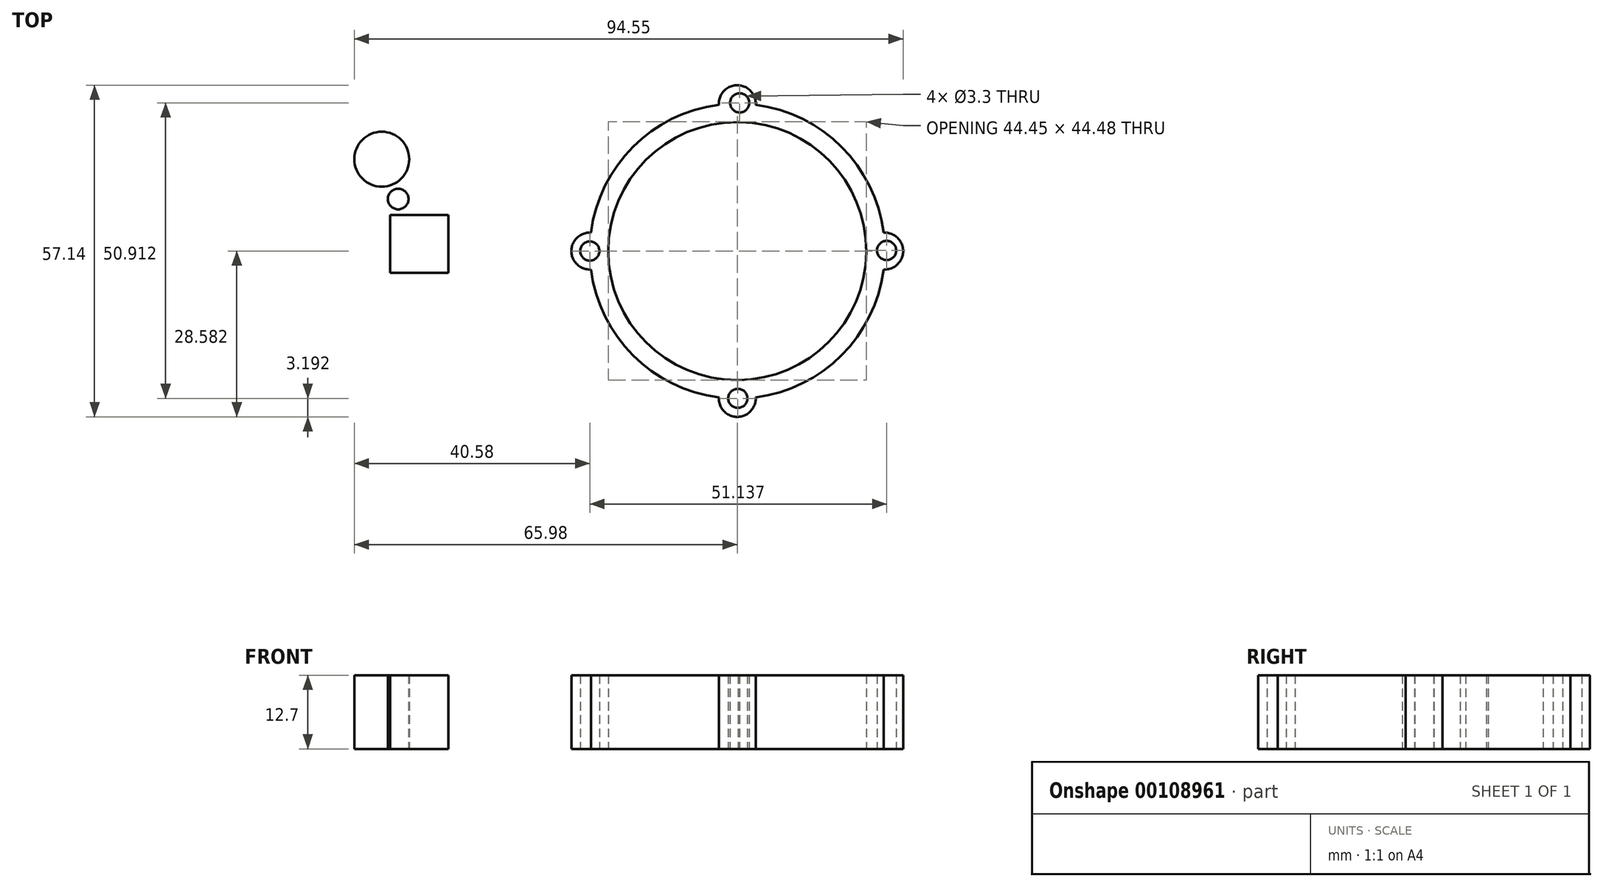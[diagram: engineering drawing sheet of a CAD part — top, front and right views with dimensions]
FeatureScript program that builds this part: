
annotation { "Feature Type Name" : "Feature", "Feature Type Description" : "" }
export const myFeature = defineFeature(function(context is Context, id is Id, definition is map)
    precondition{}
    {
        {
            var Q0;
            Q0=qCreatedBy(makeId("Top.planeOp"),FACE);
            var sketch = newSketch(context, id + "F0", { "sketchPlane" : qUnion([Q0])});
            skCircle(sketch, "E0", {"center": v(0, 0) * mm, "radius": 25.4 * mm});
            skCircle(sketch, "E1", {"center": v(0, 25.4) * mm, "radius": 3.18 * mm});
            skCircle(sketch, "E2", {"center": v(-25.4, 0) * mm, "radius": 3.18 * mm});
            skCircle(sketch, "E3", {"center": v(25.4, 0) * mm, "radius": 3.18 * mm});
            skCircle(sketch, "E4", {"center": v(0, -25.4) * mm, "radius": 3.18 * mm});
            skCircle(sketch, "E5", {"center": v(0, 0) * mm, "radius": 22.23 * mm});
            skCircle(sketch, "E6", {"center": v(-25.4, 0) * mm, "radius": 1.65 * mm});
            skCircle(sketch, "E7", {"center": v(0.1, -25.38) * mm, "radius": 1.65 * mm});
            skCircle(sketch, "E8", {"center": v(25.74, 0.11) * mm, "radius": 1.65 * mm});
            skCircle(sketch, "E9", {"center": v(0.42, 25.53) * mm, "radius": 1.65 * mm});
            skLineSegment(sketch, "E10", {"start": v(0.42, 25.53) * mm, "end": v(0.1, -25.38) * mm});
            skCircle(sketch, "E11", {"center": v(-61.24, 15.82) * mm, "radius": 4.73 * mm});
            skCircle(sketch, "E12", {"center": v(-58.4, 8.96) * mm, "radius": 1.77 * mm});
            skLineSegment(sketch, "E13.bottom", {"start": v(-59.8, 6.25) * mm, "end": v(-49.8, 6.25) * mm});
            skLineSegment(sketch, "E13.top", {"start": v(-59.8, -3.75) * mm, "end": v(-49.8, -3.75) * mm});
            skLineSegment(sketch, "E13.left", {"start": v(-59.8, 6.25) * mm, "end": v(-59.8, -3.75) * mm});
            skLineSegment(sketch, "E13.right", {"start": v(-49.8, 6.25) * mm, "end": v(-49.8, -3.75) * mm});
            skSolve(sketch);
        }
        {
            var Q0;
            Q0=qSketchRegion(id+"F0",true);
            extrude(context, id + "F1", {"entities" : qUnion([Q0]), "depth" : 12.7 * mm});
        }
    });
